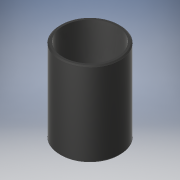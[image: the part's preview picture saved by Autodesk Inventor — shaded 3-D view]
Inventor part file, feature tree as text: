
AUTODESK INVENTOR PART (.ipt)
format: ipt  version: 2019 (Build 230136000, 136)  size: 109,056 bytes
history: native  units: mm
features: chamfer x2, extrude x1, sketch x1
ambient origin geometry x8: Origin, YZ Plane, XZ Plane, XY Plane, X Axis, Y Axis, Z Axis, Center Point
bodies: Solid1 (feature_tree)
feature tree (4):
  extrude  "Extrusion1"  Depth=14.0mm
  chamfer  "Chamfer1"  Distance=14.0mm
  chamfer  "Chamfer2"  Distance=0.2mm Angle=45.0deg
  sketch  "Sketch1"  dims[d0=10.0mm d1=9.0mm d2=14.0mm d3=0.0mm d4=0.2mm d5=2.0mm d6=45.0deg d7=0.2mm d8=2.0mm d9=45.0deg]
